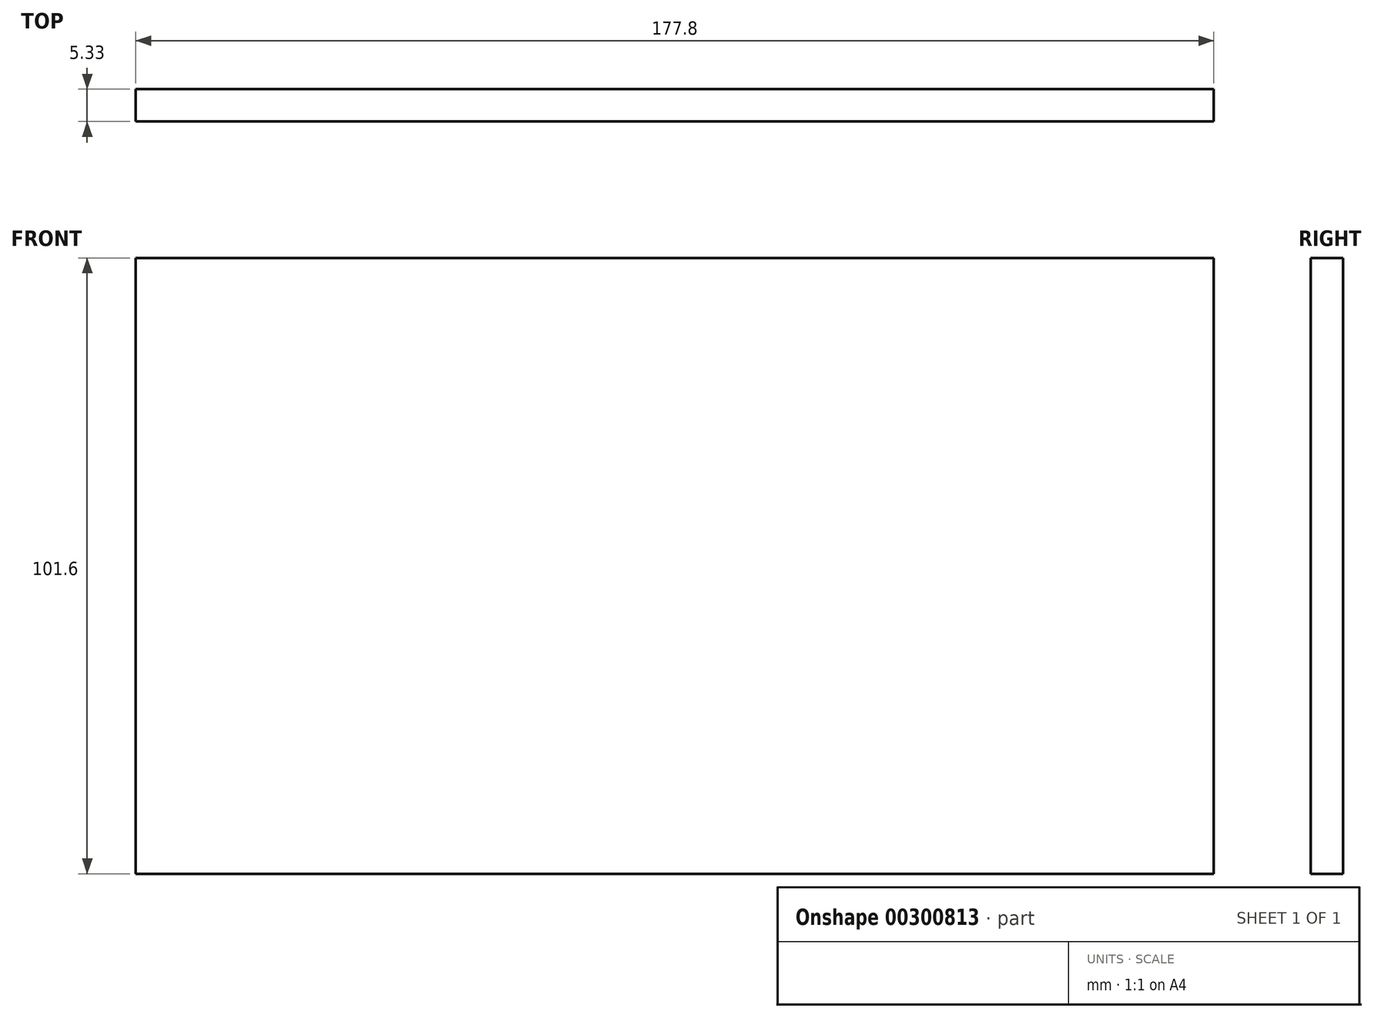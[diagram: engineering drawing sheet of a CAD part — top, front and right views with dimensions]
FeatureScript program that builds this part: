
annotation { "Feature Type Name" : "Feature", "Feature Type Description" : "" }
export const myFeature = defineFeature(function(context is Context, id is Id, definition is map)
    precondition{}
    {
        {
            var Q0;
            Q0=qCreatedBy(makeId("Front.planeOp"),FACE);
            var sketch = newSketch(context, id + "F0", { "sketchPlane" : qUnion([Q0])});
            skLineSegment(sketch, "E0.bottom", {"start": v(-73.7, 1.95) * mm, "end": v(104.1, 1.95) * mm});
            skLineSegment(sketch, "E0.top", {"start": v(-73.7, 103.55) * mm, "end": v(104.1, 103.55) * mm});
            skLineSegment(sketch, "E0.left", {"start": v(-73.7, 1.95) * mm, "end": v(-73.7, 103.55) * mm});
            skLineSegment(sketch, "E0.right", {"start": v(104.1, 1.95) * mm, "end": v(104.1, 103.55) * mm});
            skSolve(sketch);
        }
        {
            var Q0;
            Q0 = qSketchRegion(id + "F0", true);
            extrude(context, id + "F1", {"entities" : qUnion([Q0]), "depth" : 5.33 * mm});
        }
    });
